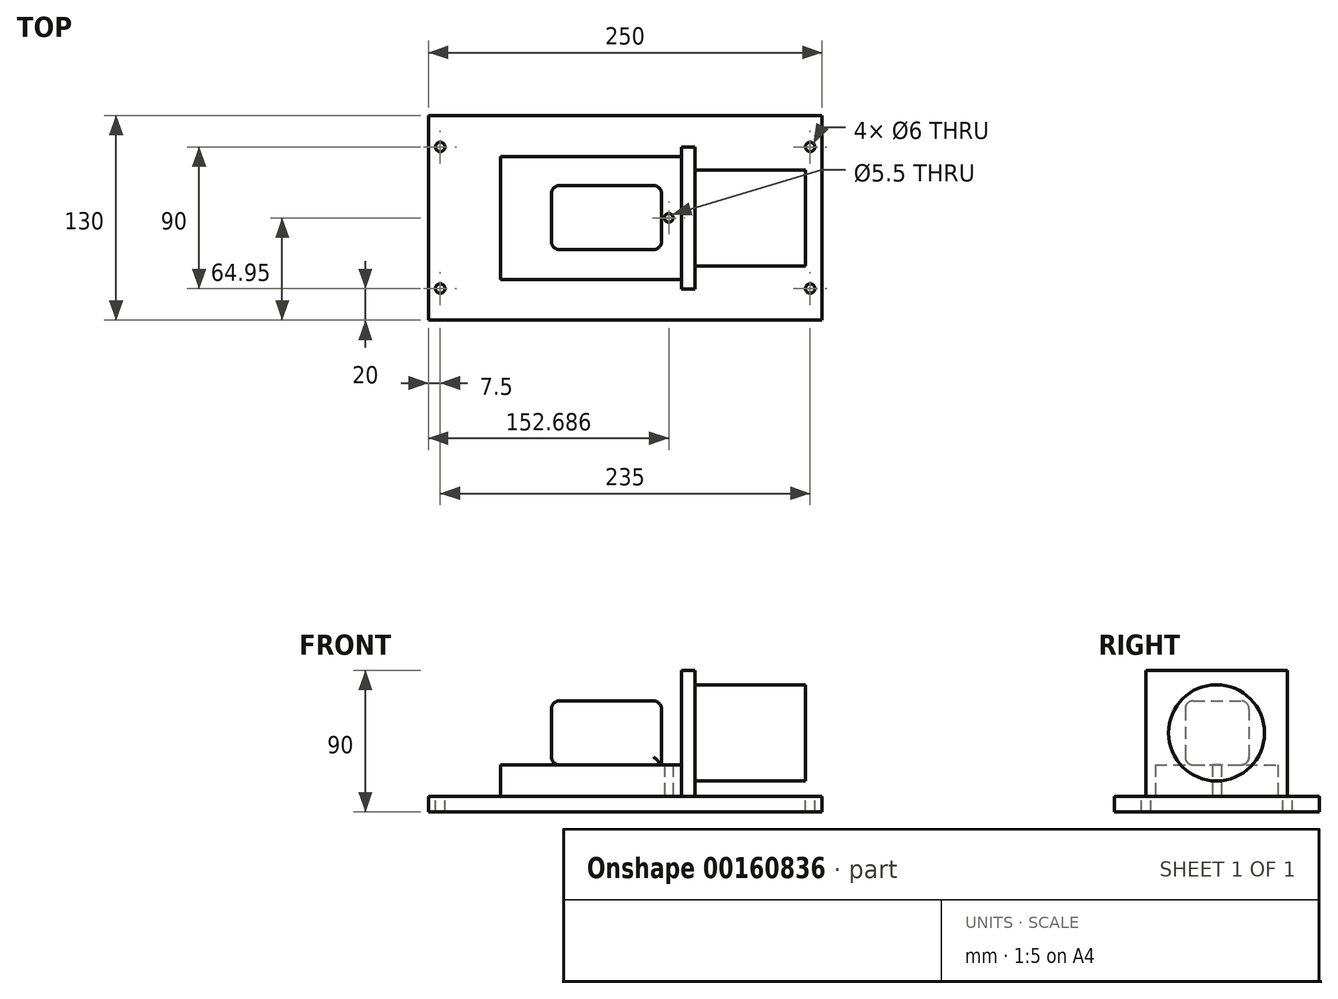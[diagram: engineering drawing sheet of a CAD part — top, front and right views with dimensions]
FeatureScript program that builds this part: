
annotation { "Feature Type Name" : "Feature", "Feature Type Description" : "" }
export const myFeature = defineFeature(function(context is Context, id is Id, definition is map)
    precondition{}
    {
        {
            var Q0;
            Q0=qCreatedBy(makeId("Top.planeOp"),FACE);
            var sketch = newSketch(context, id + "F0", { "sketchPlane" : qUnion([Q0])});
            skLineSegment(sketch, "E0.bottom", {"start": v(0, 0) * mm, "end": v(250, 0) * mm});
            skLineSegment(sketch, "E0.top", {"start": v(0, 130) * mm, "end": v(250, 130) * mm});
            skLineSegment(sketch, "E0.left", {"start": v(0, 0) * mm, "end": v(0, 130) * mm});
            skLineSegment(sketch, "E0.right", {"start": v(250, 0) * mm, "end": v(250, 130) * mm});
            skLineSegment(sketch, "E1", {"start": v(125, -4.5) * mm, "end": v(125, 141.77) * mm, "construction": true});
            skLineSegment(sketch, "E2", {"start": v(7.5, 136.62) * mm, "end": v(7.5, -18.5) * mm, "construction": true});
            skLineSegment(sketch, "E3", {"start": v(242.5, 137.2) * mm, "end": v(242.5, -15.06) * mm, "construction": true});
            skCircle(sketch, "E4", {"center": v(7.5, 110) * mm, "radius": 3 * mm});
            skCircle(sketch, "E5", {"center": v(7.5, 20) * mm, "radius": 3 * mm});
            skCircle(sketch, "E6", {"center": v(242.5, 20) * mm, "radius": 3 * mm});
            skCircle(sketch, "E7", {"center": v(242.5, 110) * mm, "radius": 3 * mm});
            skSolve(sketch);
        }
        {
            var Q0;
            Q0=makeQuery(id+"F0.imprint","IMPRINT",FACE,{"disambiguationData":[TD([[makeQuery(id+"F0.imprint","IMPRINT",EDGE,{"derivedFrom":sQuery(id+"F0.wireOp",EDGE,"E0.bottom")}),1.0]])]});
            var Q1;
            Q1=sQuery(id+"F0.wireOp",EDGE,"E0.top");
            var Q2;
            Q2=sQuery(id+"F0.wireOp",EDGE,"E0.bottom");
            var Q3;
            Q3=sQuery(id+"F0.wireOp",EDGE,"E0.left");
            var Q4;
            Q4=sQuery(id+"F0.wireOp",EDGE,"E0.right");
            extrude(context, id + "F1", {"entities" : qUnion([Q0]), "surfaceEntities" : qUnion([Q1, Q2, Q3, Q4]), "oppositeDirection" : true, "depth" : 10 * mm});
        }
        {
            var Q0;
            Q0=qCreatedBy(makeId("Top.planeOp"),FACE);
            var sketch = newSketch(context, id + "F2", { "sketchPlane" : qUnion([Q0])});
            skLineSegment(sketch, "E8.rect.bottom", {"start": v(45.99, 103.72) * mm, "end": v(160.7, 103.72) * mm});
            skLineSegment(sketch, "E8.rect.top", {"start": v(45.99, 25.85) * mm, "end": v(160.7, 25.85) * mm});
            skLineSegment(sketch, "E8.rect.left", {"start": v(45.99, 103.72) * mm, "end": v(45.99, 25.85) * mm});
            skLineSegment(sketch, "E8.rect.right", {"start": v(160.7, 103.72) * mm, "end": v(160.7, 25.85) * mm});
            skPoint(sketch, "E8.rect.middle", {"position": v(103.35, 64.78) * mm});
            skLineSegment(sketch, "E9.rect.bottom", {"start": v(169.41, 109.78) * mm, "end": v(160.7, 109.78) * mm});
            skLineSegment(sketch, "E9.rect.top", {"start": v(169.41, 19.78) * mm, "end": v(160.7, 19.78) * mm});
            skLineSegment(sketch, "E9.rect.left", {"start": v(169.41, 109.78) * mm, "end": v(169.41, 19.78) * mm});
            skLineSegment(sketch, "E9.rect.right", {"start": v(160.7, 109.78) * mm, "end": v(160.7, 19.78) * mm});
            skPoint(sketch, "E9.rect.middle", {"position": v(165.06, 64.78) * mm});
            skPoint(sketch, "E9.rect.middle.positionSnap0", {"position": v(160.7, 64.78) * mm});
            skPoint(sketch, "E9.rect.centerSnap0", {"position": v(160.7, 64.78) * mm});
            skCircle(sketch, "E10", {"center": v(152.69, 64.95) * mm, "radius": 2.75 * mm});
            skArc(sketch, "E11", {"start": v(60.94, 25.16) * mm, "mid": v(52.69, 64.83) * mm, "end": v(60.85, 104.53) * mm, "construction": true});
            skSolve(sketch);
        }
        {
            var Q0;
            Q0=qSketchRegion(id+"F2",true);
            extrude(context, id + "F3", {"entities" : qUnion([Q0]), "depth" : 20 * mm});
        }
        {
            var Q0;
            {var subQ4=sQuery(id+"F2.wireOp",EDGE,"E9.rect.bottom");Q0=makeQuery(id+"F2.imprint","IMPRINT",FACE,{"disambiguationData":[TD([[makeQuery(id+"F2.imprint","IMPRINT",EDGE,{"derivedFrom":subQ4}),1.0]])]});}
            extrude(context, id + "F4", {"entities" : qUnion([Q0]), "depth" : 80 * mm});
        }
        {
            var Q0;
            Q0=makeQuery(id+"F4.opExtrude","SWEPT_FACE",FACE,{"disambiguationData":[OSD([sQuery(id+"F2.wireOp",EDGE,"E9.rect.left")])]});
            var sketch = newSketch(context, id + "F5", { "sketchPlane" : qUnion([Q0])});
            skCircle(sketch, "E12", {"center": v(64.78, 40.3) * mm, "radius": 30.5 * mm});
            skPoint(sketch, "E13.startSnap0", {"position": v(106.07, 55.7) * mm});
            skLineSegment(sketch, "E14", {"start": v(19.78, 40) * mm, "end": v(34.29, 40) * mm});
            skLineSegment(sketch, "E15", {"start": v(95.28, 40) * mm, "end": v(109.78, 40) * mm});
            skCircle(sketch, "E16", {"center": v(34.78, 9.74) * mm, "radius": 2.75 * mm});
            skCircle(sketch, "E17", {"center": v(94.78, 9.74) * mm, "radius": 2.75 * mm});
            skLineSegment(sketch, "E18.bottom", {"start": v(19.78, 80) * mm, "end": v(109.78, 80) * mm});
            skLineSegment(sketch, "E18.top", {"start": v(19.78, 0) * mm, "end": v(109.78, 0) * mm});
            skLineSegment(sketch, "E18.left", {"start": v(19.78, 80) * mm, "end": v(19.78, 0) * mm});
            skLineSegment(sketch, "E18.right", {"start": v(109.78, 80) * mm, "end": v(109.78, 0) * mm});
            skSolve(sketch);
        }
        {
            var Q0;
            Q0=makeQuery(id+"F3.opExtrude","CAP_FACE",FACE,{"disambiguationData":[OSD([sQuery(id+"F2.wireOp",EDGE,"E8.rect.bottom"),sQuery(id+"F2.wireOp",EDGE,"E8.rect.top"),sQuery(id+"F2.wireOp",EDGE,"E8.rect.left"),sQuery(id+"F2.wireOp",EDGE,"E9.rect.bottom"),sQuery(id+"F2.wireOp",EDGE,"E9.rect.top"),sQuery(id+"F2.wireOp",EDGE,"E9.rect.left"),sQuery(id+"F2.wireOp",EDGE,"E9.rect.right")])],"isStart":false});
            var sketch = newSketch(context, id + "F6", { "sketchPlane" : qUnion([Q0])});
            skLineSegment(sketch, "E19.rect.bottom", {"start": v(148.1, 44.84) * mm, "end": v(78.1, 44.84) * mm});
            skLineSegment(sketch, "E19.rect.top", {"start": v(148.1, 85.44) * mm, "end": v(78.1, 85.44) * mm});
            skLineSegment(sketch, "E19.rect.left", {"start": v(148.1, 44.84) * mm, "end": v(148.1, 85.44) * mm});
            skLineSegment(sketch, "E19.rect.right", {"start": v(78.1, 44.84) * mm, "end": v(78.1, 85.44) * mm});
            skPoint(sketch, "E19.rect.middle", {"position": v(113.1, 65.14) * mm});
            skLineSegment(sketch, "E20.rect.bottom", {"start": v(68.03, 89.48) * mm, "end": v(148.03, 89.48) * mm});
            skLineSegment(sketch, "E20.rect.top", {"start": v(68.03, 39.48) * mm, "end": v(148.03, 39.48) * mm});
            skLineSegment(sketch, "E20.rect.left", {"start": v(68.03, 89.48) * mm, "end": v(68.03, 39.48) * mm});
            skLineSegment(sketch, "E20.rect.right", {"start": v(148.03, 89.48) * mm, "end": v(148.03, 39.48) * mm});
            skSolve(sketch);
        }
        {
            var Q0;
            {var subQ6=sQuery(id+"F6.wireOp",EDGE,"E19.rect.bottom");Q0=makeQuery(id+"F6.imprint","IMPRINT",FACE,{"disambiguationData":[TD([[makeQuery(id+"F6.imprint","IMPRINT",EDGE,{"derivedFrom":subQ6}),-1.0]])]});}
            extrude(context, id + "F7", {"entities" : qUnion([Q0]), "depth" : 40.6 * mm});
        }
        {
            var Q0;
            Q0=makeQuery(id+"F7.opExtrude","CAP_EDGE",EDGE,{"disambiguationData":[OSD([sQuery(id+"F6.wireOp",EDGE,"E19.rect.right")])],"isStart":false});
            var Q1;
            Q1=makeQuery(id+"F7.opExtrude","CAP_EDGE",EDGE,{"disambiguationData":[OSD([sQuery(id+"F6.wireOp",EDGE,"E19.rect.top")])],"isStart":false});
            var Q2;
            Q2=makeQuery(id+"F7.opExtrude","CAP_EDGE",EDGE,{"disambiguationData":[OSD([sQuery(id+"F6.wireOp",EDGE,"E19.rect.bottom")])],"isStart":false});
            var Q3;
            Q3=makeQuery(id+"F7.opExtrude","CAP_EDGE",EDGE,{"disambiguationData":[OSD([sQuery(id+"F6.wireOp",EDGE,"E19.rect.left")])],"isStart":false});
            var Q4;
            Q4=makeQuery(id+"F7.opExtrude","SWEPT_EDGE",EDGE,{"disambiguationData":[OSD([sQuery(id+"F6.wireOp",EDGE,"E19.rect.bottom"),sQuery(id+"F6.wireOp",EDGE,"E19.rect.left")])]});
            var Q5;
            Q5=makeQuery(id+"F7.opExtrude","CAP_EDGE",EDGE,{"disambiguationData":[OSD([sQuery(id+"F6.wireOp",EDGE,"E19.rect.bottom")])],"isStart":true});
            var Q6;
            Q6=makeQuery(id+"F7.opExtrude","SWEPT_EDGE",EDGE,{"disambiguationData":[OSD([sQuery(id+"F6.wireOp",EDGE,"E19.rect.bottom"),sQuery(id+"F6.wireOp",EDGE,"E19.rect.right")])]});
            var Q7;
            Q7=makeQuery(id+"F7.opExtrude","CAP_EDGE",EDGE,{"disambiguationData":[OSD([sQuery(id+"F6.wireOp",EDGE,"E19.rect.right")])],"isStart":true});
            var Q8;
            Q8=makeQuery(id+"F7.opExtrude","SWEPT_EDGE",EDGE,{"disambiguationData":[OSD([sQuery(id+"F6.wireOp",EDGE,"E19.rect.top"),sQuery(id+"F6.wireOp",EDGE,"E19.rect.right")])]});
            var Q9;
            Q9=makeQuery(id+"F7.opExtrude","CAP_EDGE",EDGE,{"disambiguationData":[OSD([sQuery(id+"F6.wireOp",EDGE,"E19.rect.top")])],"isStart":true});
            var Q10;
            Q10=makeQuery(id+"F7.opExtrude","SWEPT_EDGE",EDGE,{"disambiguationData":[OSD([sQuery(id+"F6.wireOp",EDGE,"E19.rect.top"),sQuery(id+"F6.wireOp",EDGE,"E19.rect.left")])]});
            fillet(context, id + "F8", {"entities" : qUnion([Q0, Q1, Q2, Q3, Q4, Q5, Q6, Q7, Q8, Q9, Q10]), "radius" : 5 * mm, "tangentPropagation" : true, "allowEdgeOverflow" : false});
        }
        {
            var Q0;
            {var subQ0=sQuery(id+"F5.wireOp",EDGE,"f1b0c51c-3681-4bdd-94da-034aca585fa9");var subQ1=sQuery(id+"F5.wireOp",EDGE,"E12");var subQ3=makeQuery(id+"F5.imprint","INTERSECT",VERTEX,{"disambiguationData":[OD(0.0)],"derivedFrom":[subQ1,subQ0]});Q0=makeQuery(id+"F5.imprint","IMPRINT",FACE,{"disambiguationData":[TD([[makeQuery(id+"F5.imprint","IMPRINT",EDGE,{"disambiguationData":[TD([[subQ3,-1.0]])],"derivedFrom":subQ1}),1.0]])]});}
            var Q1;
            {var subQ0=sQuery(id+"F5.wireOp",EDGE,"f1b0c51c-3681-4bdd-94da-034aca585fa9");var subQ1=sQuery(id+"F5.wireOp",EDGE,"E12");var subQ3=makeQuery(id+"F5.imprint","INTERSECT",VERTEX,{"disambiguationData":[OD(0.0)],"derivedFrom":[subQ1,subQ0]});Q1=makeQuery(id+"F5.imprint","IMPRINT",FACE,{"disambiguationData":[TD([[makeQuery(id+"F5.imprint","IMPRINT",EDGE,{"disambiguationData":[TD([[subQ3,1.0]])],"derivedFrom":subQ1}),1.0]])]});}
            var Q2;
            Q2=sQuery(id+"F5.wireOp",EDGE,"E12");
            extrude(context, id + "F9", {"entities" : qUnion([Q0, Q1]), "operationType" : NewBodyOperationType.ADD, "surfaceEntities" : qUnion([Q2]), "depth" : 70 * mm});
        }
    });
